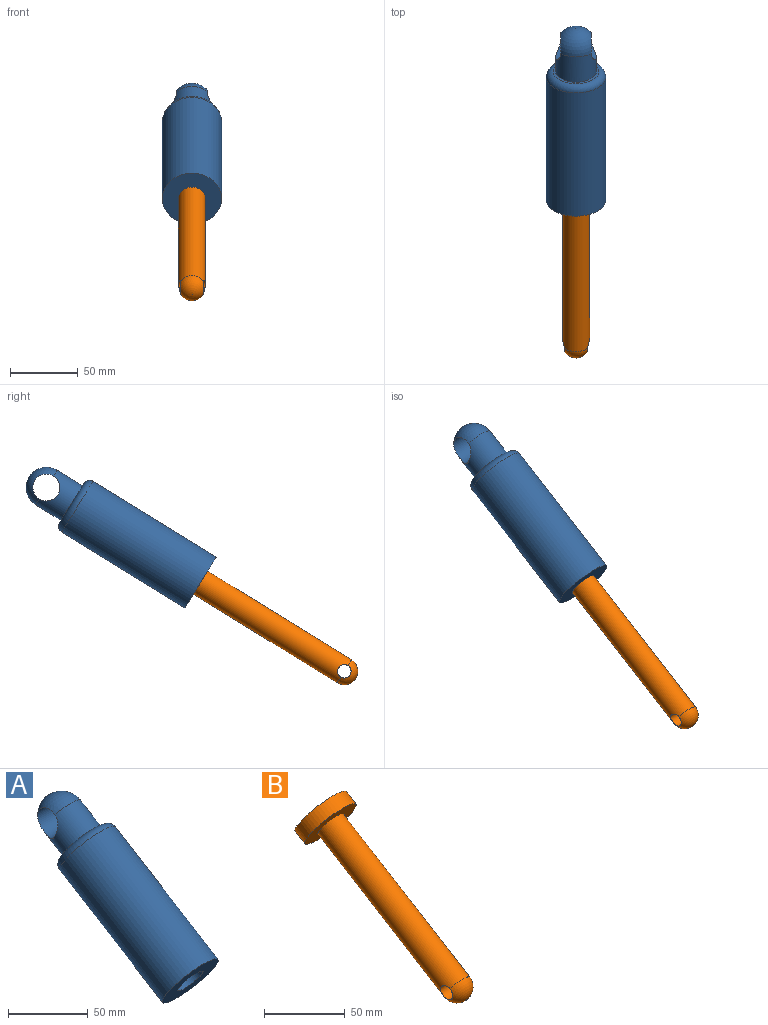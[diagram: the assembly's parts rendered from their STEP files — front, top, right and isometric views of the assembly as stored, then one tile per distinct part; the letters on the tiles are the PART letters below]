
ASSEMBLY  parts=2 mates=1
PART A: 11 faces, bbox 47.6x140.6x104.1 mm
  f0: cylinder r=15mm len=37.08mm, axis (0,-0.85,-0.52), area 1738mm2, adj f1,f8,f9
  f1: plane 34x28.94mm, normal (0,0.85,0.52), area 201.1mm2, adj f0,f10
  f2: cylinder r=22mm len=114.17mm, axis (0,-0.85,-0.52), area 14790.6mm2, adj f3,f10
  f3: plane 44x37.45mm, normal (0,-0.85,-0.52), area 1206.4mm2, adj f2,f4
  f4: cylinder r=10mm len=20mm, axis (0,-0.85,-0.52), area 314.2mm2, adj f3,f5
  f5: plane 40x34.04mm, normal (0,0.85,0.52), area 942.5mm2, adj f4,f6
  f6: cylinder r=20mm len=110.37mm, axis (0,-0.85,-0.52), area 13194.7mm2, adj f5,f7
  f7: plane 40x34.04mm, normal (0,-0.85,-0.52), area 1256.6mm2, adj f6
  f8: sphere r=15mm, area 1053.7mm2, adj f0,f9
  f9: cylinder r=10mm len=30mm, axis (1,0,0), area 1529.3mm2, adj f0,f8
  f10: torus R=17mm, axis (0,-0.85,-0.52), area 996mm2, adj f1,f2
PART B: 6 faces, bbox 40x139.7x100.5 mm
  f0: cylinder r=10mm len=121.14mm, axis (0,-0.85,-0.52), area 8086.9mm2, adj f1,f4,f5
  f1: sphere r=10mm, area 544.1mm2, adj f0,f5
  f2: plane 40x34.04mm, normal (0,0.85,0.52), area 1256.6mm2, adj f3
  f3: cylinder r=20mm len=40mm, axis (0,-0.85,-0.52), area 1256.6mm2, adj f2,f4
  f4: plane 40x34.04mm, normal (0,-0.85,-0.52), area 942.5mm2, adj f0,f3
  f5: cylinder r=5mm len=20mm, axis (1,0,0), area 565.6mm2, adj f0,f1
PLACE A rot(axis=(-0.17,0.82,0.55),0deg) t=(-211.42,452.17,-290.3)mm
PLACE B t=(-211.42,447.91,-292.92)mm
MATE slider B.f0 <-> A.f10  axis (0,-0.85,-0.52) through (-211.42,-169.09,-30.67)mm
